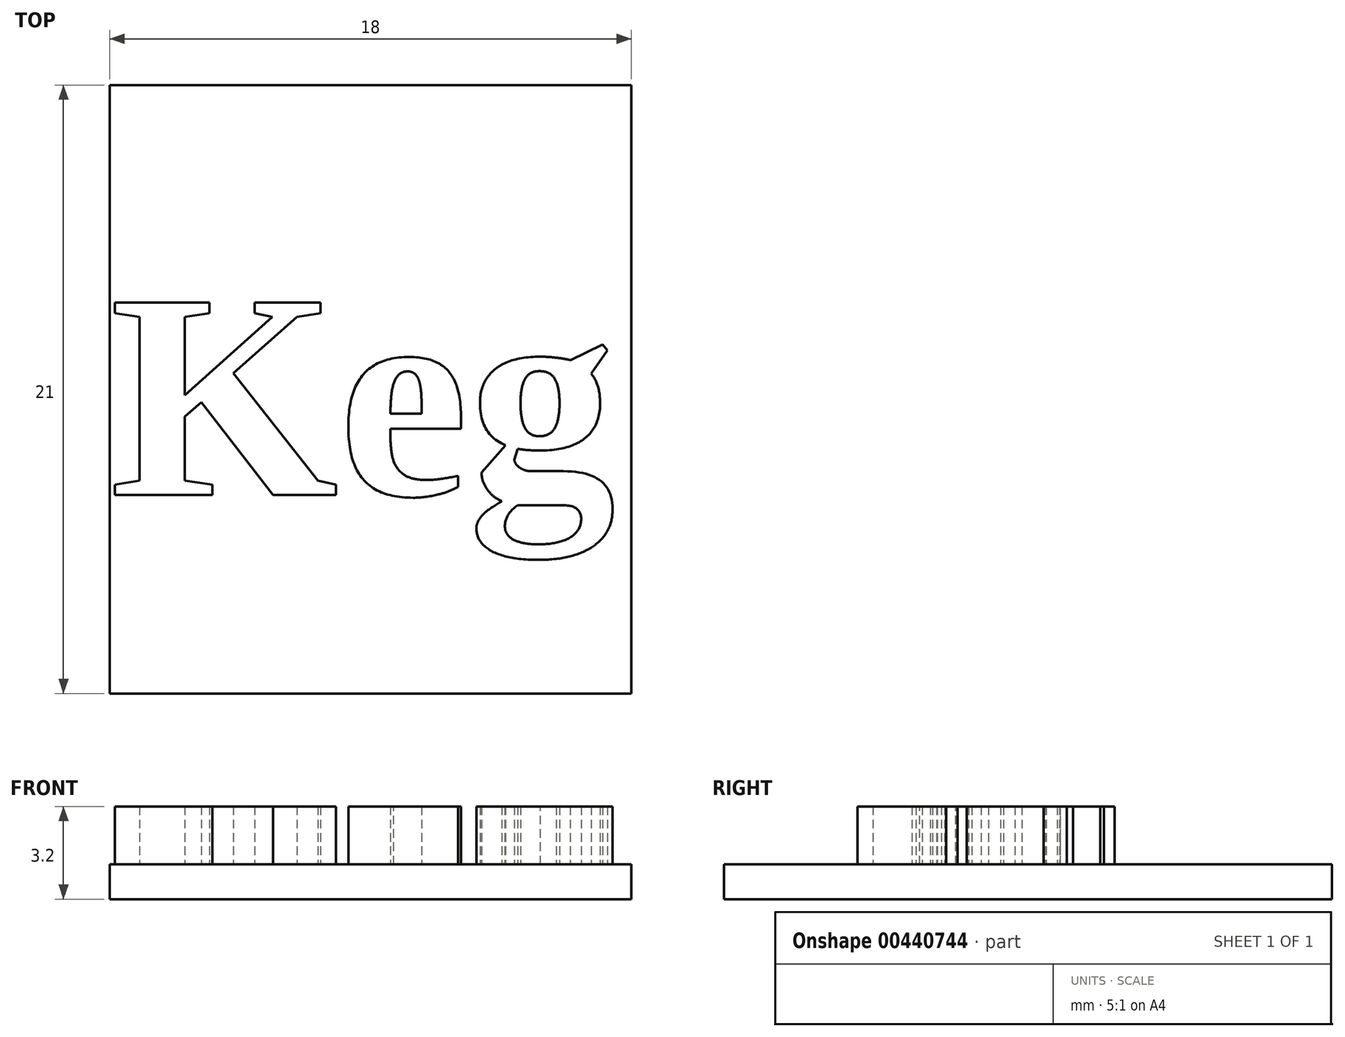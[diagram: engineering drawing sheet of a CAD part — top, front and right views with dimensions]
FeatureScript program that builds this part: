
annotation { "Feature Type Name" : "Feature", "Feature Type Description" : "" }
export const myFeature = defineFeature(function(context is Context, id is Id, definition is map)
    precondition{}
    {
        {
            var Q0;
            Q0=qCreatedBy(makeId("Top.planeOp"),FACE);
            var sketch = newSketch(context, id + "F0", { "sketchPlane" : qUnion([Q0])});
            skLineSegment(sketch, "E0.bottom", {"start": v(0, 0) * mm, "end": v(18, 0) * mm});
            skLineSegment(sketch, "E0.top", {"start": v(0, 21) * mm, "end": v(18, 21) * mm});
            skLineSegment(sketch, "E0.left", {"start": v(0, 0) * mm, "end": v(0, 21) * mm});
            skLineSegment(sketch, "E0.right", {"start": v(18, 0) * mm, "end": v(18, 21) * mm});
            skSolve(sketch);
        }
        {
            var Q0;
            Q0 = qSketchRegion(id + "F0", true);
            extrude(context, id + "F1", {"entities" : qUnion([Q0]), "depth" : 1.2 * mm});
        }
        {
            var Q0;
            Q0=makeQuery(id+"F1.opExtrude","CAP_FACE",FACE,{"disambiguationData":[OSD([sQuery(id+"F0.wireOp",EDGE,"E0.bottom"),sQuery(id+"F0.wireOp",EDGE,"E0.top"),sQuery(id+"F0.wireOp",EDGE,"E0.left"),sQuery(id+"F0.wireOp",EDGE,"E0.right")])],"isStart":false});
            var sketch = newSketch(context, id + "F2", { "sketchPlane" : qUnion([Q0])});
            skText(sketch, "E1", { "text": "Keg", "fontName": "Tinos-Bold.ttf"});
            const initialGuessF2  = {"E1": [0, 0.00685, 1, 0, 0.0073]};
            skSetInitialGuess(sketch, initialGuessF2);
            skSolve(sketch);
        }
        {
            var Q0;
            Q0 = qSketchRegion(id + "F2", true);
            extrude(context, id + "F3", {"entities" : qUnion([Q0]), "operationType" : NewBodyOperationType.ADD, "depth" : 2 * mm});
        }
    });
